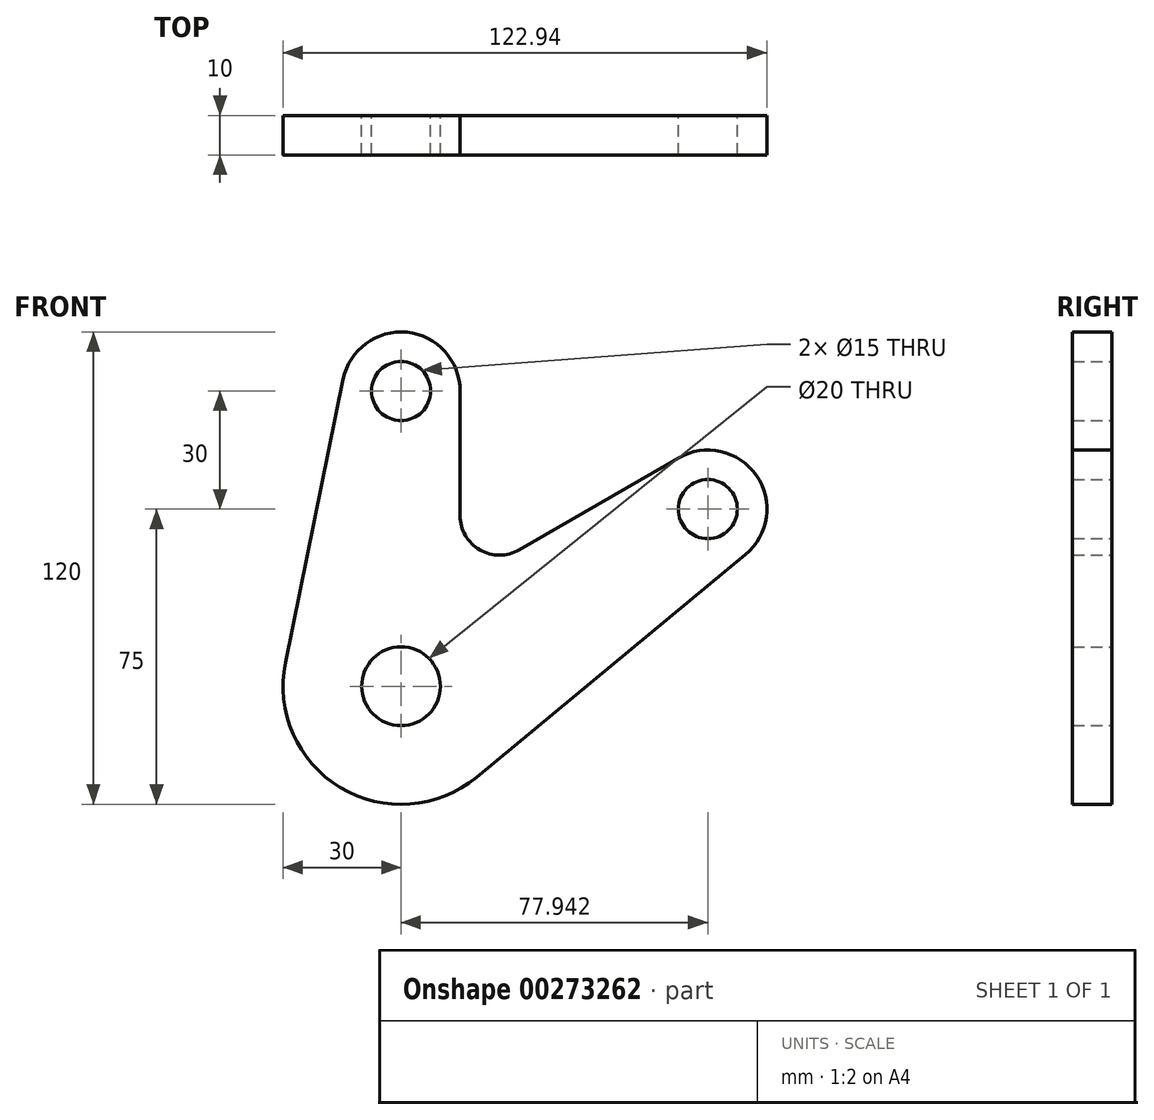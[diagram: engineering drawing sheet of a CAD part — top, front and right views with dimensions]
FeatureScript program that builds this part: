
annotation { "Feature Type Name" : "Feature", "Feature Type Description" : "" }
export const myFeature = defineFeature(function(context is Context, id is Id, definition is map)
    precondition{}
    {
        {
            var Q0;
            Q0=qCreatedBy(makeId("Front.planeOp"),FACE);
            var sketch = newSketch(context, id + "F0", { "sketchPlane" : qUnion([Q0])});
            skArc(sketch, "E0", {"start": v(-29.4, 6) * mm, "mid": v(-15.44, -25.72) * mm, "end": v(19.12, -23.12) * mm});
            skCircle(sketch, "E1", {"center": v(0, 0) * mm, "radius": 10 * mm});
            skCircle(sketch, "E2", {"center": v(0, 75) * mm, "radius": 7.5 * mm});
            skArc(sketch, "E3", {"start": v(15, 75) * mm, "mid": v(1.5, 89.92) * mm, "end": v(-14.7, 78) * mm});
            skCircle(sketch, "E4", {"center": v(77.94, 45) * mm, "radius": 7.5 * mm});
            skArc(sketch, "E5", {"start": v(87.5, 33.44) * mm, "mid": v(90.26, 53.56) * mm, "end": v(70.44, 58) * mm});
            skLineSegment(sketch, "E6", {"start": v(77.94, 45) * mm, "end": v(70.44, 58) * mm});
            skLineSegment(sketch, "E7", {"start": v(70.44, 58) * mm, "end": v(30, 34.64) * mm});
            skLineSegment(sketch, "E8", {"start": v(15, 75) * mm, "end": v(15, 43.3) * mm});
            skPoint(sketch, "E9.visualSharp", {"position": v(15, 25.98) * mm});
            skArc(sketch, "E9.filletArc", {"start": v(15, 43.3) * mm, "mid": v(20, 34.64) * mm, "end": v(30, 34.64) * mm});
            skLineSegment(sketch, "E10", {"start": v(-29.4, 6) * mm, "end": v(-14.7, 78) * mm});
            skLineSegment(sketch, "E11", {"start": v(87.5, 33.44) * mm, "end": v(19.12, -23.12) * mm});
            skLineSegment(sketch, "E12", {"start": v(0, 0) * mm, "end": v(77.94, 45) * mm, "construction": true});
            skSolve(sketch);
        }
        {
            var Q0;
            Q0=makeQuery(id+"F0.imprint","IMPRINT",FACE,{"disambiguationData":[TD([[makeQuery(id+"F0.imprint","IMPRINT",EDGE,{"derivedFrom":sQuery(id+"F0.wireOp",EDGE,"E0")}),1.0]])]});
            extrude(context, id + "F1", {"entities" : qUnion([Q0]), "depth" : 10 * mm});
        }
    });
